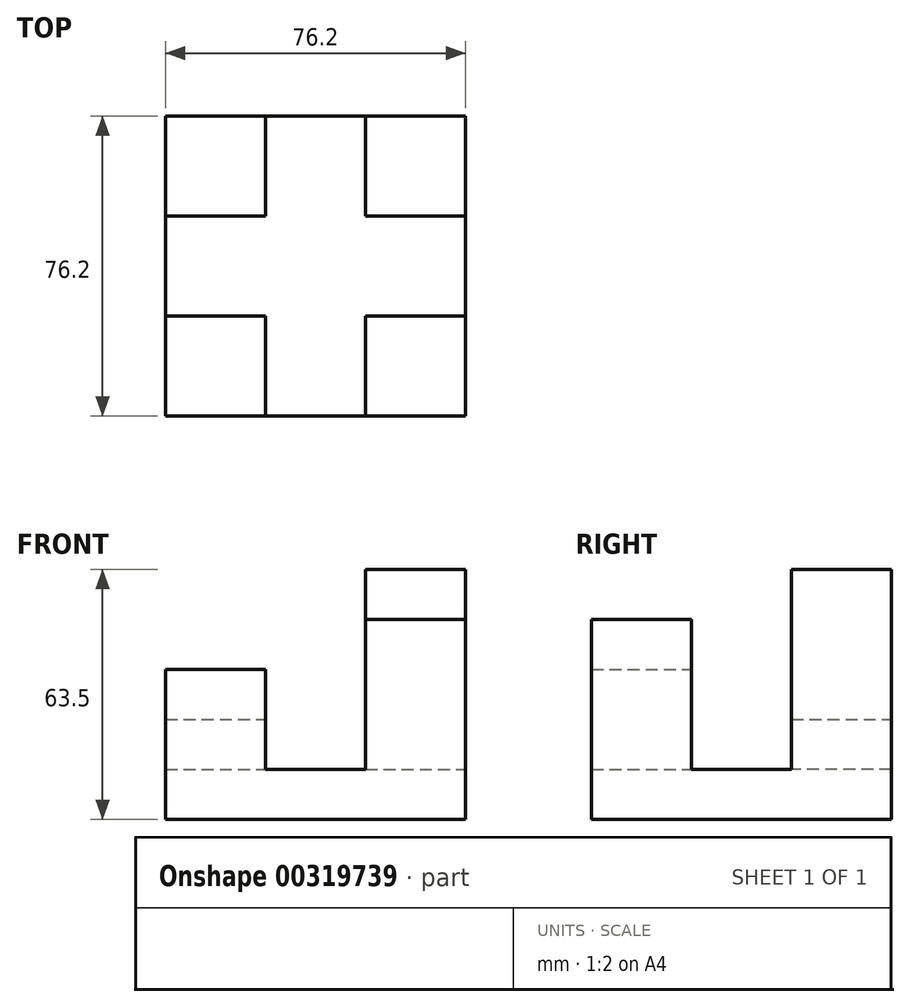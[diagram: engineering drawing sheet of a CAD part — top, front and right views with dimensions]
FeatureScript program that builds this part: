
annotation { "Feature Type Name" : "Feature", "Feature Type Description" : "" }
export const myFeature = defineFeature(function(context is Context, id is Id, definition is map)
    precondition{}
    {
        {
            var Q0;
            Q0=qCreatedBy(makeId("Top.planeOp"),FACE);
            var sketch = newSketch(context, id + "F0", { "sketchPlane" : qUnion([Q0])});
            skLineSegment(sketch, "E0", {"start": v(-33.65, 48.46) * mm, "end": v(42.55, 48.46) * mm});
            skLineSegment(sketch, "E1", {"start": v(42.55, 48.46) * mm, "end": v(42.55, -27.74) * mm});
            skLineSegment(sketch, "E2", {"start": v(42.55, -27.74) * mm, "end": v(-33.65, -27.74) * mm});
            skLineSegment(sketch, "E3", {"start": v(-33.65, -27.74) * mm, "end": v(-33.65, 48.46) * mm});
            skSolve(sketch);
        }
        {
            var Q0;
            Q0 = qSketchRegion(id + "F0", true);
            extrude(context, id + "F1", {"entities" : qUnion([Q0]), "depth" : 12.7 * mm});
        }
        {
            var Q0;
            Q0=makeQuery(id+"F1.opExtrude","CAP_FACE",FACE,{"disambiguationData":[OSD([sQuery(id+"F0.wireOp",EDGE,"E0"),sQuery(id+"F0.wireOp",EDGE,"E1"),sQuery(id+"F0.wireOp",EDGE,"E2"),sQuery(id+"F0.wireOp",EDGE,"E3")])],"isStart":false});
            var sketch = newSketch(context, id + "F2", { "sketchPlane" : qUnion([Q0])});
            skLineSegment(sketch, "E4", {"start": v(-33.65, -2.34) * mm, "end": v(-8.25, -2.34) * mm});
            skLineSegment(sketch, "E5", {"start": v(-8.25, -2.34) * mm, "end": v(-8.25, -27.74) * mm});
            skLineSegment(sketch, "E6", {"start": v(-33.65, 23.06) * mm, "end": v(-8.25, 23.06) * mm});
            skLineSegment(sketch, "E7", {"start": v(-8.25, 23.06) * mm, "end": v(-8.25, 48.46) * mm});
            skLineSegment(sketch, "E8", {"start": v(17.15, 48.46) * mm, "end": v(17.15, 23.06) * mm});
            skLineSegment(sketch, "E9", {"start": v(17.15, 23.06) * mm, "end": v(42.55, 23.06) * mm});
            skLineSegment(sketch, "E10", {"start": v(17.15, -27.74) * mm, "end": v(17.15, -2.34) * mm});
            skLineSegment(sketch, "E11", {"start": v(17.15, -2.34) * mm, "end": v(42.55, -2.34) * mm});
            skSolve(sketch);
        }
        {
            var Q0;
            {var subQ0=sQuery(id+"F2.wireOp",EDGE,"E4");Q0=makeQuery(id+"F2.imprint","IMPRINT",FACE,{"disambiguationData":[TD([[makeQuery(id+"F2.imprint","IMPRINT",EDGE,{"derivedFrom":subQ0}),-1.0]])]});}
            extrude(context, id + "F3", {"entities" : qUnion([Q0]), "operationType" : NewBodyOperationType.ADD, "depth" : 25.4 * mm});
        }
        {
            var Q0;
            {var subQ0=sQuery(id+"F2.wireOp",EDGE,"E6");Q0=makeQuery(id+"F2.imprint","IMPRINT",FACE,{"disambiguationData":[TD([[makeQuery(id+"F2.imprint","IMPRINT",EDGE,{"derivedFrom":subQ0}),1.0]])]});}
            extrude(context, id + "F4", {"entities" : qUnion([Q0]), "operationType" : NewBodyOperationType.ADD, "depth" : 12.7 * mm});
        }
        {
            var Q0;
            {var subQ0=sQuery(id+"F2.wireOp",EDGE,"E8");Q0=makeQuery(id+"F2.imprint","IMPRINT",FACE,{"disambiguationData":[TD([[makeQuery(id+"F2.imprint","IMPRINT",EDGE,{"derivedFrom":subQ0}),1.0]])]});}
            extrude(context, id + "F5", {"entities" : qUnion([Q0]), "operationType" : NewBodyOperationType.ADD, "depth" : 50.8 * mm});
        }
        {
            var Q0;
            {var subQ0=sQuery(id+"F2.wireOp",EDGE,"E10");Q0=makeQuery(id+"F2.imprint","IMPRINT",FACE,{"disambiguationData":[TD([[makeQuery(id+"F2.imprint","IMPRINT",EDGE,{"derivedFrom":subQ0}),-1.0]])]});}
            extrude(context, id + "F6", {"entities" : qUnion([Q0]), "operationType" : NewBodyOperationType.ADD, "depth" : 38.1 * mm});
        }
    });
